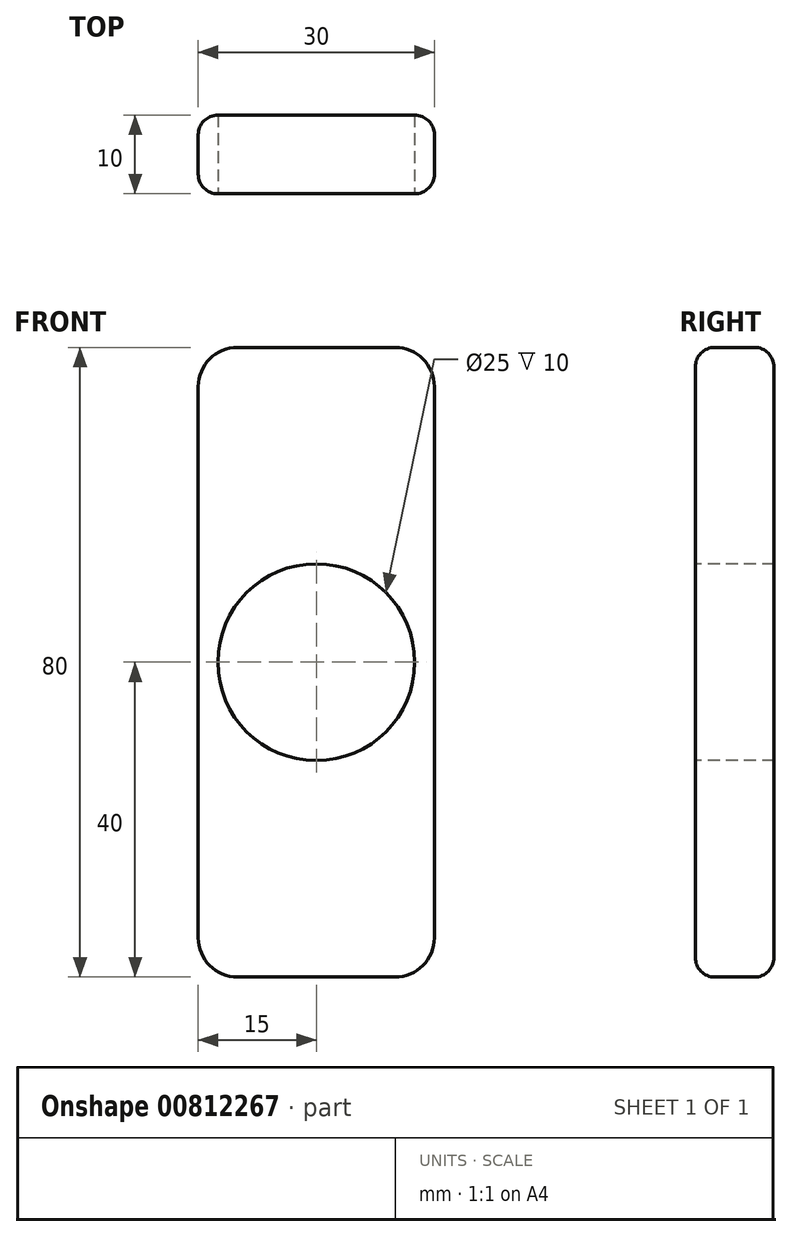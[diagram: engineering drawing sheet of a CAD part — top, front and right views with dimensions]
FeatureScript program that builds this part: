
annotation { "Feature Type Name" : "Feature", "Feature Type Description" : "" }
export const myFeature = defineFeature(function(context is Context, id is Id, definition is map)
    precondition{}
    {
        {
            var Q0;
            Q0=qCreatedBy(makeId("Front.planeOp"),FACE);
            var sketch = newSketch(context, id + "F0", { "sketchPlane" : qUnion([Q0])});
            skLineSegment(sketch, "E0.bottom", {"start": v(0, 0) * mm, "end": v(30, 0) * mm});
            skLineSegment(sketch, "E0.top", {"start": v(0, 80) * mm, "end": v(30, 80) * mm});
            skLineSegment(sketch, "E0.left", {"start": v(0, 0) * mm, "end": v(0, 80) * mm});
            skLineSegment(sketch, "E0.right", {"start": v(30, 0) * mm, "end": v(30, 80) * mm});
            skSolve(sketch);
        }
        {
            var Q0;
            Q0=makeQuery(id+"F0.imprint","IMPRINT",FACE,{"disambiguationData":[TD([[makeQuery(id+"F0.imprint","IMPRINT",EDGE,{"derivedFrom":sQuery(id+"F0.wireOp",EDGE,"E0.bottom")}),1.0]])]});
            extrude(context, id + "F1", {"entities" : qUnion([Q0]), "depth" : 10 * mm, "offsetDistance" : 25 * mm});
        }
        {
            var Q0;
            Q0=makeQuery(id+"F1.opExtrude","SWEPT_EDGE",EDGE,{"disambiguationData":[OSD([sQuery(id+"F0.wireOp",EDGE,"E0.top"),sQuery(id+"F0.wireOp",EDGE,"E0.right")])]});
            fillet(context, id + "F2", {"entities" : qUnion([Q0]), "radius" : 5 * mm, "tangentPropagation" : true, "allowEdgeOverflow" : false});
        }
        {
            var Q0;
            Q0=makeQuery(id+"F1.opExtrude","SWEPT_EDGE",EDGE,{"disambiguationData":[OSD([sQuery(id+"F0.wireOp",EDGE,"E0.top"),sQuery(id+"F0.wireOp",EDGE,"E0.left")])]});
            fillet(context, id + "F3", {"entities" : qUnion([Q0]), "radius" : 5 * mm, "tangentPropagation" : true, "allowEdgeOverflow" : false});
        }
        {
            var Q0;
            Q0=makeQuery(id+"F1.opExtrude","SWEPT_EDGE",EDGE,{"disambiguationData":[OSD([sQuery(id+"F0.wireOp",EDGE,"E0.bottom"),sQuery(id+"F0.wireOp",EDGE,"E0.left")])]});
            fillet(context, id + "F4", {"entities" : qUnion([Q0]), "radius" : 5 * mm, "tangentPropagation" : true, "allowEdgeOverflow" : false});
        }
        {
            var Q0;
            Q0=makeQuery(id+"F1.opExtrude","SWEPT_EDGE",EDGE,{"disambiguationData":[OSD([sQuery(id+"F0.wireOp",EDGE,"E0.bottom"),sQuery(id+"F0.wireOp",EDGE,"E0.right")])]});
            fillet(context, id + "F5", {"entities" : qUnion([Q0]), "radius" : 5 * mm, "tangentPropagation" : true, "allowEdgeOverflow" : false});
        }
        {
            var Q0;
            {var subQ0=sQuery(id+"F0.wireOp",EDGE,"E0.right");var subQ1=sQuery(id+"F0.wireOp",EDGE,"E0.top");Q0=makeQuery(id+"F2.opFillet","BLEND_EDGE",EDGE,{"blendedFrom":[makeQuery(id+"F1.opExtrude","SWEPT_EDGE",EDGE,{"disambiguationData":[OSD([subQ1,subQ0])]}),makeQuery(id+"F1.opExtrude","CAP_FACE",FACE,{"disambiguationData":[OSD([sQuery(id+"F0.wireOp",EDGE,"E0.bottom"),subQ1,sQuery(id+"F0.wireOp",EDGE,"E0.left"),subQ0])],"isStart":false})],"blendedInto":[makeQuery(id+"F1.opExtrude","CAP_FACE",FACE,{"disambiguationData":[OSD([sQuery(id+"F0.wireOp",EDGE,"E0.bottom"),subQ1,sQuery(id+"F0.wireOp",EDGE,"E0.left"),subQ0])],"isStart":false})]});}
            fillet(context, id + "F6", {"entities" : qUnion([Q0]), "radius" : 2.5 * mm, "tangentPropagation" : true, "allowEdgeOverflow" : false});
        }
        {
            var Q0;
            {var subQ0=sQuery(id+"F0.wireOp",EDGE,"E0.right");var subQ1=sQuery(id+"F0.wireOp",EDGE,"E0.top");Q0=makeQuery(id+"F2.opFillet","BLEND_EDGE",EDGE,{"blendedFrom":[makeQuery(id+"F1.opExtrude","SWEPT_EDGE",EDGE,{"disambiguationData":[OSD([subQ1,subQ0])]}),makeQuery(id+"F1.opExtrude","CAP_FACE",FACE,{"disambiguationData":[OSD([sQuery(id+"F0.wireOp",EDGE,"E0.bottom"),subQ1,sQuery(id+"F0.wireOp",EDGE,"E0.left"),subQ0])],"isStart":true})],"blendedInto":[makeQuery(id+"F1.opExtrude","CAP_FACE",FACE,{"disambiguationData":[OSD([sQuery(id+"F0.wireOp",EDGE,"E0.bottom"),subQ1,sQuery(id+"F0.wireOp",EDGE,"E0.left"),subQ0])],"isStart":true})]});}
            fillet(context, id + "F7", {"entities" : qUnion([Q0]), "radius" : 2.5 * mm, "tangentPropagation" : true, "allowEdgeOverflow" : false});
        }
        {
            var Q0;
            Q0=makeQuery(id+"F1.opExtrude","CAP_FACE",FACE,{"disambiguationData":[OSD([sQuery(id+"F0.wireOp",EDGE,"E0.bottom"),sQuery(id+"F0.wireOp",EDGE,"E0.top"),sQuery(id+"F0.wireOp",EDGE,"E0.left"),sQuery(id+"F0.wireOp",EDGE,"E0.right")])],"isStart":false});
            var sketch = newSketch(context, id + "F8", { "sketchPlane" : qUnion([Q0])});
            skCircle(sketch, "E1", {"center": v(15, 40) * mm, "radius": 12.5 * mm});
            skPoint(sketch, "E2", {"position": v(15, 77.5) * mm});
            skPoint(sketch, "E3", {"position": v(27.5, 40) * mm});
            skSolve(sketch);
        }
        {
            var Q0;
            Q0=sQuery(id+"F8.wireOp",VERTEX,"E1.center");
            var Q1;
            Q1=makeQuery(id+"F1.opExtrude","SWEPT_BODY",BODY,{"disambiguationData":[OSD([sQuery(id+"F0.wireOp",EDGE,"E0.bottom"),sQuery(id+"F0.wireOp",EDGE,"E0.top"),sQuery(id+"F0.wireOp",EDGE,"E0.left"),sQuery(id+"F0.wireOp",EDGE,"E0.right")])]});
            hole(context, id + "F9", {"style" : HoleStyle.SIMPLE, "endStyle" : HoleEndStyle.THROUGH, "holeDiameter" : 25 * mm, "majorDiameter" : 5 * mm, "isTappedThrough" : true, "tappedDepth" : 12 * mm, "tapClearance" : 3, "locations" : qUnion([Q0]), "scope" : qUnion([Q1])});
        }
    });
